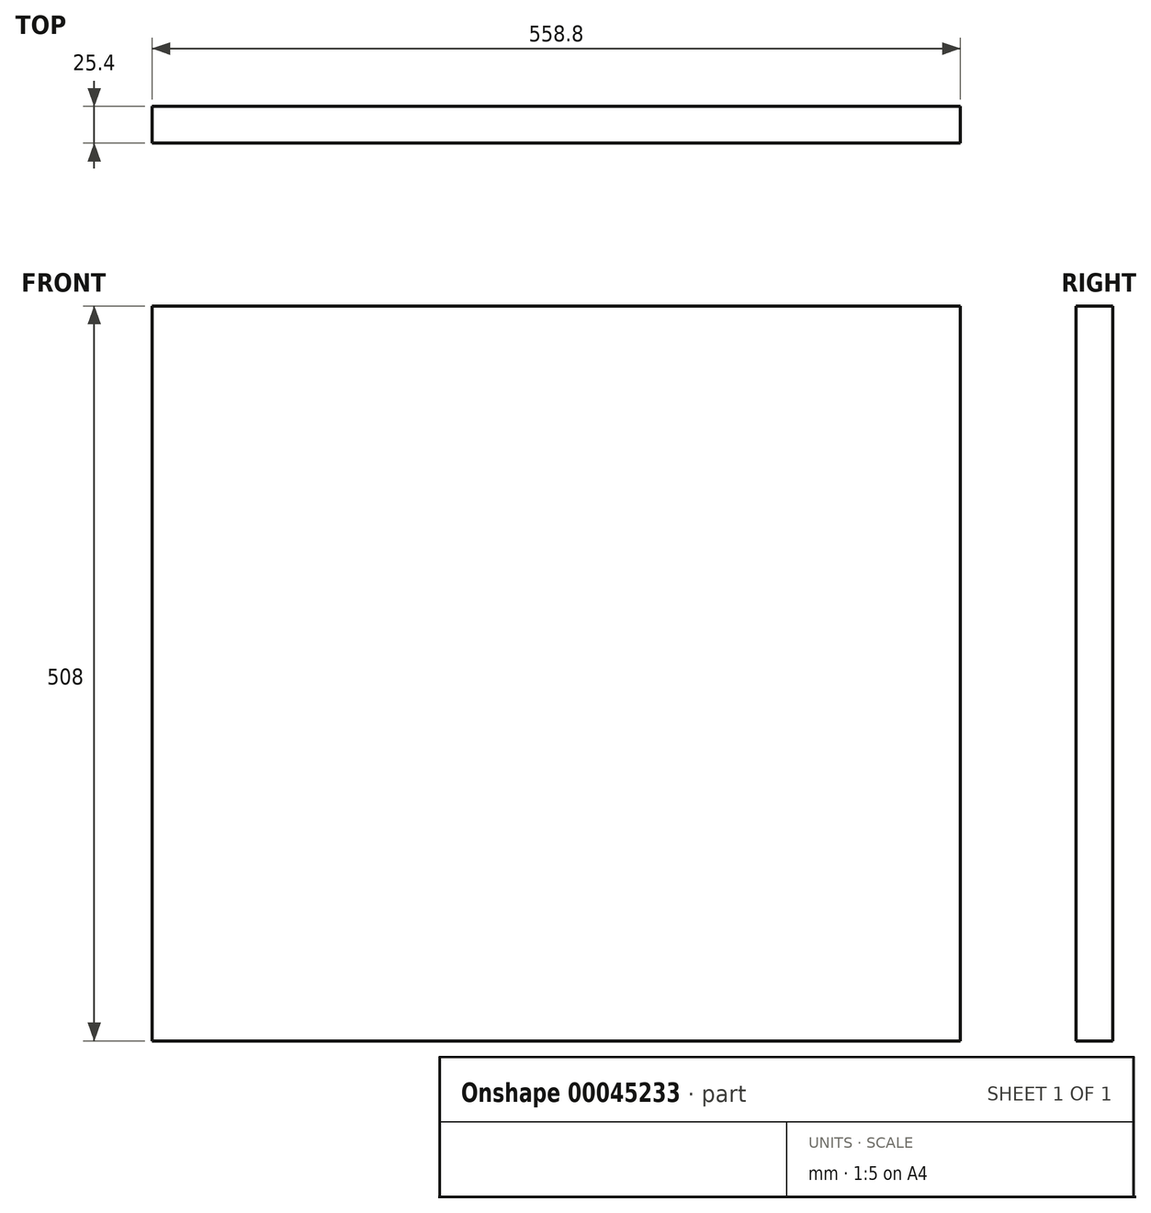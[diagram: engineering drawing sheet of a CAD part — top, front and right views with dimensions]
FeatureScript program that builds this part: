
annotation { "Feature Type Name" : "Feature", "Feature Type Description" : "" }
export const myFeature = defineFeature(function(context is Context, id is Id, definition is map)
    precondition{}
    {
        {
            var Q0;
            Q0=qCreatedBy(makeId("Front.planeOp"),FACE);
            var sketch = newSketch(context, id + "F0", { "sketchPlane" : qUnion([Q0])});
            skLineSegment(sketch, "E0.rect.bottom", {"start": v(279.4, -254) * mm, "end": v(-279.4, -254) * mm});
            skLineSegment(sketch, "E0.rect.top", {"start": v(279.4, 254) * mm, "end": v(-279.4, 254) * mm});
            skLineSegment(sketch, "E0.rect.left", {"start": v(279.4, -254) * mm, "end": v(279.4, 254) * mm});
            skLineSegment(sketch, "E0.rect.right", {"start": v(-279.4, -254) * mm, "end": v(-279.4, 254) * mm});
            skPoint(sketch, "E0.rect.middle", {"position": v(0, 0) * mm});
            skSolve(sketch);
        }
        {
            var Q0;
            Q0=makeQuery(id+"F0.imprint","IMPRINT",FACE,{"disambiguationData":[TD([[makeQuery(id+"F0.imprint","IMPRINT",EDGE,{"derivedFrom":sQuery(id+"F0.wireOp",EDGE,"E0.rect.bottom")}),-1.0]])]});
            extrude(context, id + "F1", {"entities" : qUnion([Q0]), "depth" : 25.4 * mm});
        }
    });
